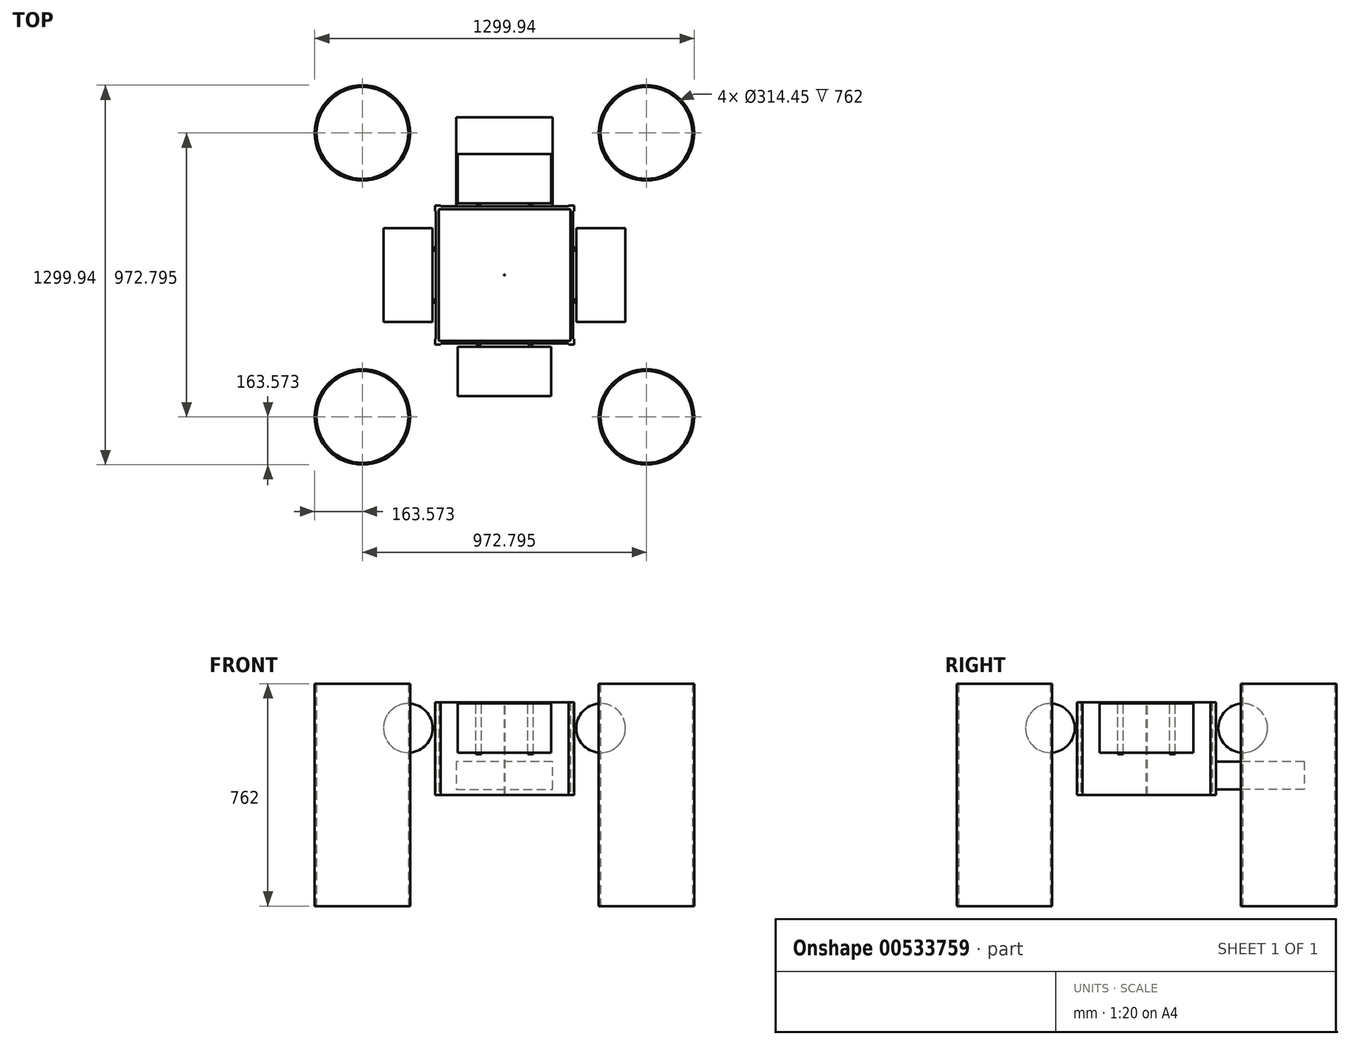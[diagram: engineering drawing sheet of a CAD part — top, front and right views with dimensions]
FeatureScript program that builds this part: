
annotation { "Feature Type Name" : "Feature", "Feature Type Description" : "" }
export const myFeature = defineFeature(function(context is Context, id is Id, definition is map)
    precondition{}
    {
        {
            var Q0;
            Q0=qCreatedBy(makeId("Top.planeOp"),FACE);
            var sketch = newSketch(context, id + "F0", { "sketchPlane" : qUnion([Q0])});
            skLineSegment(sketch, "E0.bottom", {"start": v(234.95, -234.95) * mm, "end": v(-234.95, -234.95) * mm});
            skLineSegment(sketch, "E0.top", {"start": v(234.95, 234.95) * mm, "end": v(-234.95, 234.95) * mm});
            skLineSegment(sketch, "E0.left", {"start": v(234.95, -234.95) * mm, "end": v(234.95, 234.95) * mm});
            skLineSegment(sketch, "E0.right", {"start": v(-234.95, -234.95) * mm, "end": v(-234.95, 234.95) * mm});
            skPoint(sketch, "E0.middle", {"position": v(0, 0) * mm});
            skLineSegment(sketch, "E1", {"start": v(-234.95, 238.13) * mm, "end": v(-238.13, 238.13) * mm});
            skLineSegment(sketch, "E2.bottom", {"start": v(-238.13, 238.13) * mm, "end": v(-219.08, 238.13) * mm});
            skLineSegment(sketch, "E2.top", {"start": v(-234.95, 234.95) * mm, "end": v(-219.08, 234.95) * mm});
            skLineSegment(sketch, "E2.left", {"start": v(-238.13, 238.13) * mm, "end": v(-238.13, 234.95) * mm});
            skLineSegment(sketch, "E2.right", {"start": v(-219.08, 238.13) * mm, "end": v(-219.08, 234.95) * mm});
            skLineSegment(sketch, "E3.bottom", {"start": v(-238.13, 238.13) * mm, "end": v(-234.95, 238.13) * mm});
            skLineSegment(sketch, "E3.top", {"start": v(-238.13, 219.08) * mm, "end": v(-234.95, 219.08) * mm});
            skLineSegment(sketch, "E3.left", {"start": v(-238.13, 238.13) * mm, "end": v(-238.13, 219.08) * mm});
            skLineSegment(sketch, "E3.right", {"start": v(-234.95, 234.95) * mm, "end": v(-234.95, 219.08) * mm});
            skLineSegment(sketch, "E4.1.0", {"start": v(-234.95, -234.95) * mm, "end": v(-219.08, -234.95) * mm});
            skLineSegment(sketch, "E4.1.1", {"start": v(-238.13, -238.13) * mm, "end": v(-219.08, -238.13) * mm});
            skLineSegment(sketch, "E4.1.2", {"start": v(-238.13, -238.13) * mm, "end": v(-238.13, -219.08) * mm});
            skLineSegment(sketch, "E4.1.3", {"start": v(-234.95, -234.95) * mm, "end": v(-234.95, -219.08) * mm});
            skLineSegment(sketch, "E4.1.4", {"start": v(-238.13, -219.08) * mm, "end": v(-234.95, -219.08) * mm});
            skLineSegment(sketch, "E4.1.5", {"start": v(-219.08, -238.13) * mm, "end": v(-219.08, -234.95) * mm});
            skLineSegment(sketch, "E4.1.6", {"start": v(-238.13, -238.13) * mm, "end": v(-234.95, -238.13) * mm});
            skLineSegment(sketch, "E4.1.7", {"start": v(-238.13, -238.13) * mm, "end": v(-238.13, -234.95) * mm});
            skLineSegment(sketch, "E4.1.8", {"start": v(-238.13, -234.95) * mm, "end": v(-238.13, -238.13) * mm});
            skLineSegment(sketch, "E4.2.0", {"start": v(234.95, -234.95) * mm, "end": v(234.95, -219.08) * mm});
            skLineSegment(sketch, "E4.2.1", {"start": v(238.13, -238.13) * mm, "end": v(238.13, -219.08) * mm});
            skLineSegment(sketch, "E4.2.2", {"start": v(238.13, -238.13) * mm, "end": v(219.08, -238.13) * mm});
            skLineSegment(sketch, "E4.2.3", {"start": v(234.95, -234.95) * mm, "end": v(219.08, -234.95) * mm});
            skLineSegment(sketch, "E4.2.4", {"start": v(219.08, -238.13) * mm, "end": v(219.08, -234.95) * mm});
            skLineSegment(sketch, "E4.2.5", {"start": v(238.13, -219.08) * mm, "end": v(234.95, -219.08) * mm});
            skLineSegment(sketch, "E4.2.6", {"start": v(238.13, -238.13) * mm, "end": v(238.13, -234.95) * mm});
            skLineSegment(sketch, "E4.2.7", {"start": v(238.13, -238.13) * mm, "end": v(234.95, -238.13) * mm});
            skLineSegment(sketch, "E4.2.8", {"start": v(234.95, -238.13) * mm, "end": v(238.13, -238.13) * mm});
            skLineSegment(sketch, "E4.3.0", {"start": v(234.95, 234.95) * mm, "end": v(219.08, 234.95) * mm});
            skLineSegment(sketch, "E4.3.1", {"start": v(238.13, 238.13) * mm, "end": v(219.08, 238.13) * mm});
            skLineSegment(sketch, "E4.3.2", {"start": v(238.13, 238.13) * mm, "end": v(238.13, 219.08) * mm});
            skLineSegment(sketch, "E4.3.3", {"start": v(234.95, 234.95) * mm, "end": v(234.95, 219.08) * mm});
            skLineSegment(sketch, "E4.3.4", {"start": v(238.13, 219.08) * mm, "end": v(234.95, 219.08) * mm});
            skLineSegment(sketch, "E4.3.5", {"start": v(219.08, 238.13) * mm, "end": v(219.08, 234.95) * mm});
            skLineSegment(sketch, "E4.3.6", {"start": v(238.13, 238.13) * mm, "end": v(234.95, 238.13) * mm});
            skLineSegment(sketch, "E4.3.7", {"start": v(238.13, 238.13) * mm, "end": v(238.13, 234.95) * mm});
            skLineSegment(sketch, "E4.3.8", {"start": v(238.13, 234.95) * mm, "end": v(238.13, 238.13) * mm});
            skLineSegment(sketch, "E5.0", {"start": v(225.43, 225.43) * mm, "end": v(-225.42, 225.42) * mm});
            skLineSegment(sketch, "E5.1", {"start": v(225.43, -225.42) * mm, "end": v(225.43, 225.42) * mm});
            skLineSegment(sketch, "E5.2", {"start": v(225.43, -225.42) * mm, "end": v(-225.42, -225.43) * mm});
            skLineSegment(sketch, "E5.3", {"start": v(-225.42, -225.43) * mm, "end": v(-225.42, 225.42) * mm});
            skSolve(sketch);
        }
        {
            var Q0;
            Q0 = qSketchRegion(id + "F0", true);
            extrude(context, id + "F1", {"entities" : qUnion([Q0]), "depth" : 317.5 * mm, "offsetDistance" : 25.4 * mm});
        }
        {
            var Q0;
            Q0=qCreatedBy(makeId("Right.planeOp"),FACE);
            var sketch = newSketch(context, id + "F2", { "sketchPlane" : qUnion([Q0])});
            skLineSegment(sketch, "E6", {"start": v(234.95, 0) * mm, "end": v(234.95, 228.6) * mm});
            skLineSegment(sketch, "E7", {"start": v(234.95, 228.6) * mm, "end": v(330.2, 228.6) * mm});
            skCircle(sketch, "E8", {"center": v(330.2, 228.6) * mm, "radius": 84.14 * mm});
            skSolve(sketch);
        }
        {
            var Q0;
            Q0 = qSketchRegion(id + "F2", true);
            extrude(context, id + "F3", {"entities" : qUnion([Q0]), "endBound" : BoundingType.SYMMETRIC, "depth" : 320.67 * mm, "offsetDistance" : 25.4 * mm});
        }
        {
            var Q0;
            Q0=makeQuery(id+"F1.opExtrude","CAP_FACE",FACE,{"disambiguationData":[OSD([sQuery(id+"F0.wireOp",EDGE,"E0.bottom"),sQuery(id+"F0.wireOp",EDGE,"E0.top"),sQuery(id+"F0.wireOp",EDGE,"E0.left"),sQuery(id+"F0.wireOp",EDGE,"E0.right"),sQuery(id+"F0.wireOp",EDGE,"E2.bottom"),sQuery(id+"F0.wireOp",EDGE,"E2.right"),sQuery(id+"F0.wireOp",EDGE,"E3.bottom"),sQuery(id+"F0.wireOp",EDGE,"E3.top"),sQuery(id+"F0.wireOp",EDGE,"E3.left"),sQuery(id+"F0.wireOp",EDGE,"E4.1.1"),sQuery(id+"F0.wireOp",EDGE,"E4.1.2"),sQuery(id+"F0.wireOp",EDGE,"E4.1.4"),sQuery(id+"F0.wireOp",EDGE,"E4.1.5"),sQuery(id+"F0.wireOp",EDGE,"E4.1.6"),sQuery(id+"F0.wireOp",EDGE,"E4.1.8"),sQuery(id+"F0.wireOp",EDGE,"E4.2.1"),sQuery(id+"F0.wireOp",EDGE,"E4.2.2"),sQuery(id+"F0.wireOp",EDGE,"E4.2.4"),sQuery(id+"F0.wireOp",EDGE,"E4.2.5"),sQuery(id+"F0.wireOp",EDGE,"E4.2.6"),sQuery(id+"F0.wireOp",EDGE,"E4.2.8"),sQuery(id+"F0.wireOp",EDGE,"E4.3.1"),sQuery(id+"F0.wireOp",EDGE,"E4.3.2"),sQuery(id+"F0.wireOp",EDGE,"E4.3.4"),sQuery(id+"F0.wireOp",EDGE,"E4.3.5"),sQuery(id+"F0.wireOp",EDGE,"E4.3.6"),sQuery(id+"F0.wireOp",EDGE,"E4.3.8"),sQuery(id+"F0.wireOp",EDGE,"E5.0"),sQuery(id+"F0.wireOp",EDGE,"E5.1"),sQuery(id+"F0.wireOp",EDGE,"E5.2"),sQuery(id+"F0.wireOp",EDGE,"E5.3")])],"isStart":false});
            var sketch = newSketch(context, id + "F4", { "sketchPlane" : qUnion([Q0])});
            skLineSegment(sketch, "E9", {"start": v(0, 234.95) * mm, "end": v(-79.38, 234.95) * mm});
            skLineSegment(sketch, "E10", {"start": v(-79.38, 234.95) * mm, "end": v(-79.38, 238.12) * mm});
            skLineSegment(sketch, "E11", {"start": v(-79.38, 238.12) * mm, "end": v(-98.43, 238.12) * mm});
            skLineSegment(sketch, "E12", {"start": v(-98.43, 238.12) * mm, "end": v(-98.43, 234.95) * mm});
            skLineSegment(sketch, "E13", {"start": v(-98.43, 234.95) * mm, "end": v(-79.38, 234.95) * mm});
            skLineSegment(sketch, "E14", {"start": v(0, 234.95) * mm, "end": v(0, 171.04) * mm});
            skPoint(sketch, "E14.endSnap0", {"position": v(0, 225.42) * mm});
            skLineSegment(sketch, "E15.MirrorCS", {"start": v(79.37, 234.95) * mm, "end": v(79.37, 238.12) * mm});
            skLineSegment(sketch, "E16.MirrorCS", {"start": v(98.43, 238.12) * mm, "end": v(98.43, 234.95) * mm});
            skLineSegment(sketch, "E17.MirrorCS", {"start": v(0, 234.95) * mm, "end": v(79.38, 234.95) * mm});
            skLineSegment(sketch, "E18.MirrorCS", {"start": v(79.38, 238.13) * mm, "end": v(98.43, 238.13) * mm});
            skLineSegment(sketch, "E19.MirrorCS", {"start": v(98.43, 234.95) * mm, "end": v(79.38, 234.95) * mm});
            skSolve(sketch);
        }
        {
            var Q0;
            Q0 = qSketchRegion(id + "F4", true);
            extrude(context, id + "F5", {"entities" : qUnion([Q0]), "oppositeDirection" : true, "depth" : 177.8 * mm, "offsetDistance" : 25.4 * mm});
        }
        {
            var Q0;
            Q0=qCreatedBy(makeId("Top.planeOp"),FACE);
            var sketch = newSketch(context, id + "F6", { "sketchPlane" : qUnion([Q0])});
            skCircle(sketch, "E20", {"center": v(0, 0) * mm, "radius": 1.59 * mm});
            skSolve(sketch);
        }
        {
            var Q0;
            Q0 = qSketchRegion(id + "F6", true);
            extrude(context, id + "F7", {"entities" : qUnion([Q0]), "depth" : 304.8 * mm, "offsetDistance" : 25.4 * mm});
        }
        {
            var Q0;
            Q0=makeQuery(id+"F3.opExtrude","SWEPT_BODY",BODY,{"disambiguationData":[OSD([sQuery(id+"F2.wireOp",EDGE,"E8")])]});
            var Q1;
            Q1=makeQuery(id+"F5.opExtrude","SWEPT_BODY",BODY,{"disambiguationData":[OSD([sQuery(id+"F4.wireOp",EDGE,"E10"),sQuery(id+"F4.wireOp",EDGE,"E11"),sQuery(id+"F4.wireOp",EDGE,"E12"),sQuery(id+"F4.wireOp",EDGE,"E13")])]});
            var Q2;
            Q2=makeQuery(id+"F5.opExtrude","SWEPT_BODY",BODY,{"disambiguationData":[OSD([sQuery(id+"F4.wireOp",EDGE,"E15.MirrorCS"),sQuery(id+"F4.wireOp",EDGE,"E16.MirrorCS"),sQuery(id+"F4.wireOp",EDGE,"E18.MirrorCS"),sQuery(id+"F4.wireOp",EDGE,"E19.MirrorCS")])]});
            var Q3;
            Q3=makeQuery(id+"F7.opExtrude","SWEPT_FACE",FACE,{"disambiguationData":[OSD([sQuery(id+"F6.wireOp",EDGE,"E20")])]});
            circularPattern(context, id + "F8", {"entities" : qUnion([Q0, Q1, Q2]), "axis" : qUnion([Q3]), "angle" : 360 * degree, "instanceCount" : 4, "equalSpace" : true});
        }
        {
            var Q0;
            Q0=makeQuery(id+"F1.opExtrude","SWEPT_FACE",FACE,{"disambiguationData":[OSD([sQuery(id+"F0.wireOp",EDGE,"E0.top")])]});
            var sketch = newSketch(context, id + "F9", { "sketchPlane" : qUnion([Q0])});
            skLineSegment(sketch, "E21", {"start": v(0, 0) * mm, "end": v(0, 19.05) * mm});
            skPoint(sketch, "E21.endSnap0", {"position": v(0, 0) * mm});
            skLineSegment(sketch, "E22", {"start": v(0, 19.05) * mm, "end": v(165.1, 19.05) * mm});
            skLineSegment(sketch, "E23.MirrorCS", {"start": v(0, 19.05) * mm, "end": v(-165.1, 19.05) * mm});
            skLineSegment(sketch, "E24", {"start": v(-165.1, 19.05) * mm, "end": v(-165.1, 114.3) * mm});
            skLineSegment(sketch, "E25", {"start": v(-165.1, 114.3) * mm, "end": v(165.1, 114.3) * mm});
            skLineSegment(sketch, "E26", {"start": v(165.1, 114.3) * mm, "end": v(165.1, 19.05) * mm});
            skSolve(sketch);
        }
        {
            var Q0;
            Q0 = qSketchRegion(id + "F9", true);
            extrude(context, id + "F10", {"entities" : qUnion([Q0]), "depth" : 304.8 * mm, "offsetDistance" : 25.4 * mm});
        }
        {
            var Q0;
            Q0=makeQuery(id+"F1.opExtrude","SWEPT_FACE",FACE,{"disambiguationData":[OSD([sQuery(id+"F0.wireOp",EDGE,"E4.3.2"),sQuery(id+"F0.wireOp",EDGE,"E4.3.8")])]});
            var sketch = newSketch(context, id + "F11", { "sketchPlane" : qUnion([Q0])});
            skLineSegment(sketch, "E27", {"start": v(644.53, 0) * mm, "end": v(644.53, 25.4) * mm});
            skLineSegment(sketch, "E28", {"start": v(238.13, 317.5) * mm, "end": v(314.33, 317.5) * mm});
            skArc(sketch, "E29", {"start": v(640.07, 52.43) * mm, "mid": v(524.3, 242.86) * mm, "end": v(314.33, 317.5) * mm});
            skLineSegment(sketch, "E30", {"start": v(238.13, 0) * mm, "end": v(238.13, -1.27) * mm});
            skLineSegment(sketch, "E31", {"start": v(238.13, -1.27) * mm, "end": v(219.08, -1.27) * mm});
            skArc(sketch, "E32", {"start": v(238.12, -1.27) * mm, "mid": v(428.57, 4.57) * mm, "end": v(618.3, 22.06) * mm});
            skLineSegment(sketch, "E33", {"start": v(219.08, -1.27) * mm, "end": v(219.08, 0) * mm});
            skLineSegment(sketch, "E34", {"start": v(219.08, 0) * mm, "end": v(238.13, 0) * mm});
            skLineSegment(sketch, "E35", {"start": v(238.13, 317.5) * mm, "end": v(238.13, 292.1) * mm});
            skLineSegment(sketch, "E36", {"start": v(238.13, 317.5) * mm, "end": v(263.53, 317.5) * mm});
            skLineSegment(sketch, "E37", {"start": v(238.13, 292.1) * mm, "end": v(238.13, 266.7) * mm});
            skPoint(sketch, "E38.visualSharp", {"position": v(644.52, 25.4) * mm});
            skArc(sketch, "E38.filletArc", {"start": v(618.3, 22.06) * mm, "mid": v(635.84, 32.47) * mm, "end": v(640.07, 52.43) * mm});
            skArc(sketch, "E39.0", {"start": v(238.12, 0) * mm, "mid": v(428.5, 5.83) * mm, "end": v(618.15, 23.32) * mm});
            skArc(sketch, "E39.1", {"start": v(618.15, 23.32) * mm, "mid": v(634.81, 33.21) * mm, "end": v(638.82, 52.17) * mm});
            skArc(sketch, "E39.2", {"start": v(638.82, 52.17) * mm, "mid": v(523.5, 241.87) * mm, "end": v(314.33, 316.23) * mm});
            skLineSegment(sketch, "E39.3", {"start": v(238.13, 316.23) * mm, "end": v(314.33, 316.23) * mm});
            skLineSegment(sketch, "E40", {"start": v(263.53, 317.5) * mm, "end": v(263.53, 316.23) * mm});
            skArc(sketch, "E41", {"start": v(263.53, 316.23) * mm, "mid": v(245.65, 309.62) * mm, "end": v(238.13, 292.1) * mm});
            skLineSegment(sketch, "E42", {"start": v(263.53, 316.23) * mm, "end": v(288.93, 316.23) * mm});
            skLineSegment(sketch, "E43.0", {"start": v(263.5, 314.96) * mm, "end": v(288.93, 314.96) * mm});
            skArc(sketch, "E43.1", {"start": v(263.5, 314.96) * mm, "mid": v(246.53, 308.7) * mm, "end": v(239.4, 292.1) * mm});
            skLineSegment(sketch, "E43.2", {"start": v(239.4, 292.1) * mm, "end": v(239.4, 266.7) * mm});
            skLineSegment(sketch, "E44", {"start": v(288.93, 314.96) * mm, "end": v(288.93, 316.23) * mm});
            skLineSegment(sketch, "E45", {"start": v(238.13, 266.7) * mm, "end": v(239.4, 266.7) * mm});
            skLineSegment(sketch, "E46", {"start": v(238.13, 317.5) * mm, "end": v(234.95, 317.5) * mm});
            skLineSegment(sketch, "E47", {"start": v(234.95, 317.5) * mm, "end": v(234.95, 316.23) * mm});
            skLineSegment(sketch, "E48", {"start": v(234.95, 316.23) * mm, "end": v(238.13, 316.23) * mm});
            skSolve(sketch);
        }
        {
            var Q0;
            Q0 = qSketchRegion(id + "F11", true);
            extrude(context, id + "F12", {"entities" : qUnion([Q0]), "oppositeDirection" : true, "depth" : 679.45 * mm, "offsetDistance" : 25.4 * mm, "hasSecondDirection" : true, "secondDirectionOppositeDirection" : false, "secondDirectionDepth" : 203.2 * mm});
        }
        {
            var Q0;
            Q0=qCreatedBy(makeId("Top.planeOp"),FACE);
            var sketch = newSketch(context, id + "F13", { "sketchPlane" : qUnion([Q0])});
            skLineSegment(sketch, "E49", {"start": v(0, 0) * mm, "end": v(0, 486.4) * mm});
            skLineSegment(sketch, "E50", {"start": v(0, 486.4) * mm, "end": v(486.4, 486.4) * mm});
            skCircle(sketch, "E51", {"center": v(486.4, 486.4) * mm, "radius": 157.23 * mm});
            skCircle(sketch, "E52.0", {"center": v(486.4, 486.4) * mm, "radius": 163.58 * mm});
            skCircle(sketch, "E53.1.0", {"center": v(-486.4, 486.4) * mm, "radius": 163.58 * mm});
            skCircle(sketch, "E53.1.1", {"center": v(-486.4, 486.4) * mm, "radius": 157.23 * mm});
            skCircle(sketch, "E53.2.0", {"center": v(-486.4, -486.4) * mm, "radius": 163.58 * mm});
            skCircle(sketch, "E53.2.1", {"center": v(-486.4, -486.4) * mm, "radius": 157.23 * mm});
            skCircle(sketch, "E53.3.0", {"center": v(486.4, -486.4) * mm, "radius": 163.58 * mm});
            skCircle(sketch, "E53.3.1", {"center": v(486.4, -486.4) * mm, "radius": 157.23 * mm});
            skPoint(sketch, "E53.center", {"position": v(0, 0) * mm});
            skSolve(sketch);
        }
        {
            var Q0;
            Q0 = qSketchRegion(id + "F13", true);
            extrude(context, id + "F14", {"entities" : qUnion([Q0]), "endBound" : BoundingType.SYMMETRIC, "depth" : 762 * mm, "offsetDistance" : 25.4 * mm});
        }
        {
            var Q0;
            Q0=makeQuery(id+"F14.opExtrude","SWEPT_BODY",BODY,{"disambiguationData":[OSD([sQuery(id+"F13.wireOp",EDGE,"E51"),sQuery(id+"F13.wireOp",EDGE,"E52.0")])]});
            var Q1;
            Q1=makeQuery(id+"F14.opExtrude","SWEPT_BODY",BODY,{"disambiguationData":[OSD([sQuery(id+"F13.wireOp",EDGE,"E53.1.0"),sQuery(id+"F13.wireOp",EDGE,"E53.1.1")])]});
            var Q2;
            Q2=makeQuery(id+"F12.opExtrude","SWEPT_BODY",BODY,{"disambiguationData":[OSD([sQuery(id+"F11.wireOp",EDGE,"E28"),sQuery(id+"F11.wireOp",EDGE,"E29"),sQuery(id+"F11.wireOp",EDGE,"E31"),sQuery(id+"F11.wireOp",EDGE,"E32"),sQuery(id+"F11.wireOp",EDGE,"E33"),sQuery(id+"F11.wireOp",EDGE,"E34"),sQuery(id+"F11.wireOp",EDGE,"E35"),sQuery(id+"F11.wireOp",EDGE,"E36"),sQuery(id+"F11.wireOp",EDGE,"E37"),sQuery(id+"F11.wireOp",EDGE,"E38.filletArc"),sQuery(id+"F11.wireOp",EDGE,"E39.0"),sQuery(id+"F11.wireOp",EDGE,"E39.1"),sQuery(id+"F11.wireOp",EDGE,"E39.2"),sQuery(id+"F11.wireOp",EDGE,"E39.3"),sQuery(id+"F11.wireOp",EDGE,"E41"),sQuery(id+"F11.wireOp",EDGE,"E43.0"),sQuery(id+"F11.wireOp",EDGE,"E43.1"),sQuery(id+"F11.wireOp",EDGE,"E43.2"),sQuery(id+"F11.wireOp",EDGE,"E44"),sQuery(id+"F11.wireOp",EDGE,"E45"),sQuery(id+"F11.wireOp",EDGE,"E46"),sQuery(id+"F11.wireOp",EDGE,"E47"),sQuery(id+"F11.wireOp",EDGE,"E48")])]});
            booleanBodies(context, id + "F15", {"operationType" : BooleanOperationType.SUBTRACTION, "tools" : qUnion([Q0, Q1]), "targets" : qUnion([Q2]), "keepTools" : true});
        }
        {
            var Q0;
            Q0=makeQuery(id+"F15.opBoolean","SPLIT",BODY,{"disambiguationData":[OD(1.0)],"derivedFrom":makeQuery(id+"F12.opExtrude","SWEPT_BODY",BODY,{"disambiguationData":[OSD([sQuery(id+"F11.wireOp",EDGE,"E28"),sQuery(id+"F11.wireOp",EDGE,"E29"),sQuery(id+"F11.wireOp",EDGE,"E31"),sQuery(id+"F11.wireOp",EDGE,"E32"),sQuery(id+"F11.wireOp",EDGE,"E33"),sQuery(id+"F11.wireOp",EDGE,"E34"),sQuery(id+"F11.wireOp",EDGE,"E35"),sQuery(id+"F11.wireOp",EDGE,"E36"),sQuery(id+"F11.wireOp",EDGE,"E37"),sQuery(id+"F11.wireOp",EDGE,"E38.filletArc"),sQuery(id+"F11.wireOp",EDGE,"E39.0"),sQuery(id+"F11.wireOp",EDGE,"E39.1"),sQuery(id+"F11.wireOp",EDGE,"E39.2"),sQuery(id+"F11.wireOp",EDGE,"E39.3"),sQuery(id+"F11.wireOp",EDGE,"E41"),sQuery(id+"F11.wireOp",EDGE,"E43.0"),sQuery(id+"F11.wireOp",EDGE,"E43.1"),sQuery(id+"F11.wireOp",EDGE,"E43.2"),sQuery(id+"F11.wireOp",EDGE,"E44"),sQuery(id+"F11.wireOp",EDGE,"E45"),sQuery(id+"F11.wireOp",EDGE,"E46"),sQuery(id+"F11.wireOp",EDGE,"E47"),sQuery(id+"F11.wireOp",EDGE,"E48")])]})});
            var Q1;
            Q1=makeQuery(id+"F15.opBoolean","SPLIT",BODY,{"disambiguationData":[OD(2.0)],"derivedFrom":makeQuery(id+"F12.opExtrude","SWEPT_BODY",BODY,{"disambiguationData":[OSD([sQuery(id+"F11.wireOp",EDGE,"E28"),sQuery(id+"F11.wireOp",EDGE,"E29"),sQuery(id+"F11.wireOp",EDGE,"E31"),sQuery(id+"F11.wireOp",EDGE,"E32"),sQuery(id+"F11.wireOp",EDGE,"E33"),sQuery(id+"F11.wireOp",EDGE,"E34"),sQuery(id+"F11.wireOp",EDGE,"E35"),sQuery(id+"F11.wireOp",EDGE,"E36"),sQuery(id+"F11.wireOp",EDGE,"E37"),sQuery(id+"F11.wireOp",EDGE,"E38.filletArc"),sQuery(id+"F11.wireOp",EDGE,"E39.0"),sQuery(id+"F11.wireOp",EDGE,"E39.1"),sQuery(id+"F11.wireOp",EDGE,"E39.2"),sQuery(id+"F11.wireOp",EDGE,"E39.3"),sQuery(id+"F11.wireOp",EDGE,"E41"),sQuery(id+"F11.wireOp",EDGE,"E43.0"),sQuery(id+"F11.wireOp",EDGE,"E43.1"),sQuery(id+"F11.wireOp",EDGE,"E43.2"),sQuery(id+"F11.wireOp",EDGE,"E44"),sQuery(id+"F11.wireOp",EDGE,"E45"),sQuery(id+"F11.wireOp",EDGE,"E46"),sQuery(id+"F11.wireOp",EDGE,"E47"),sQuery(id+"F11.wireOp",EDGE,"E48")])]})});
            var Q2;
            Q2=makeQuery(id+"F15.opBoolean","SPLIT",BODY,{"disambiguationData":[OD(4.0)],"derivedFrom":makeQuery(id+"F12.opExtrude","SWEPT_BODY",BODY,{"disambiguationData":[OSD([sQuery(id+"F11.wireOp",EDGE,"E28"),sQuery(id+"F11.wireOp",EDGE,"E29"),sQuery(id+"F11.wireOp",EDGE,"E31"),sQuery(id+"F11.wireOp",EDGE,"E32"),sQuery(id+"F11.wireOp",EDGE,"E33"),sQuery(id+"F11.wireOp",EDGE,"E34"),sQuery(id+"F11.wireOp",EDGE,"E35"),sQuery(id+"F11.wireOp",EDGE,"E36"),sQuery(id+"F11.wireOp",EDGE,"E37"),sQuery(id+"F11.wireOp",EDGE,"E38.filletArc"),sQuery(id+"F11.wireOp",EDGE,"E39.0"),sQuery(id+"F11.wireOp",EDGE,"E39.1"),sQuery(id+"F11.wireOp",EDGE,"E39.2"),sQuery(id+"F11.wireOp",EDGE,"E39.3"),sQuery(id+"F11.wireOp",EDGE,"E41"),sQuery(id+"F11.wireOp",EDGE,"E43.0"),sQuery(id+"F11.wireOp",EDGE,"E43.1"),sQuery(id+"F11.wireOp",EDGE,"E43.2"),sQuery(id+"F11.wireOp",EDGE,"E44"),sQuery(id+"F11.wireOp",EDGE,"E45"),sQuery(id+"F11.wireOp",EDGE,"E46"),sQuery(id+"F11.wireOp",EDGE,"E47"),sQuery(id+"F11.wireOp",EDGE,"E48")])]})});
            var Q3;
            Q3=makeQuery(id+"F15.opBoolean","SPLIT",BODY,{"disambiguationData":[OD(3.0)],"derivedFrom":makeQuery(id+"F12.opExtrude","SWEPT_BODY",BODY,{"disambiguationData":[OSD([sQuery(id+"F11.wireOp",EDGE,"E28"),sQuery(id+"F11.wireOp",EDGE,"E29"),sQuery(id+"F11.wireOp",EDGE,"E31"),sQuery(id+"F11.wireOp",EDGE,"E32"),sQuery(id+"F11.wireOp",EDGE,"E33"),sQuery(id+"F11.wireOp",EDGE,"E34"),sQuery(id+"F11.wireOp",EDGE,"E35"),sQuery(id+"F11.wireOp",EDGE,"E36"),sQuery(id+"F11.wireOp",EDGE,"E37"),sQuery(id+"F11.wireOp",EDGE,"E38.filletArc"),sQuery(id+"F11.wireOp",EDGE,"E39.0"),sQuery(id+"F11.wireOp",EDGE,"E39.1"),sQuery(id+"F11.wireOp",EDGE,"E39.2"),sQuery(id+"F11.wireOp",EDGE,"E39.3"),sQuery(id+"F11.wireOp",EDGE,"E41"),sQuery(id+"F11.wireOp",EDGE,"E43.0"),sQuery(id+"F11.wireOp",EDGE,"E43.1"),sQuery(id+"F11.wireOp",EDGE,"E43.2"),sQuery(id+"F11.wireOp",EDGE,"E44"),sQuery(id+"F11.wireOp",EDGE,"E45"),sQuery(id+"F11.wireOp",EDGE,"E46"),sQuery(id+"F11.wireOp",EDGE,"E47"),sQuery(id+"F11.wireOp",EDGE,"E48")])]})});
            deleteBodies(context, id + "F16", {"entities" : qUnion([Q0, Q1, Q2, Q3])});
        }
    });
